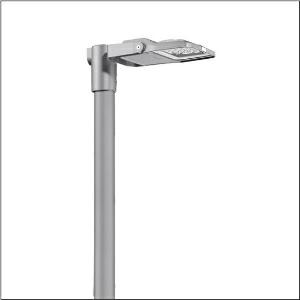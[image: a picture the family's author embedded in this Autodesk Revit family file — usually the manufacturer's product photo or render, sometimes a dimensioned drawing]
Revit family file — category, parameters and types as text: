
# Revit family: floodlight_fl_21_iq_micro___pl43_5xa7761a4a3a_9f97
name_source: partatom
category: Lighting Fixtures
units: mm (PartAtom-declared; Revit-internal decimal feet)

## family parameters
Cut with Voids When Loaded = No
Host = Face
Light Source = No
Part Type = Normal
Room Calculation Point = No
Round Connector Dimension = Use Diameter
Shared = No

## types (1)
- --- (1 x LED, 3170 lm, 23.1 W, 4000K)
    Apparent Load = 23 VA
    CIE Flux Codes = 29 80 99 100 100
    Color Rendering = 70
    Color Temperature = 4000K
    Default Elevation = 1800 mm
    Description = Floodlight FL 21 iQ micro, floodlight, primary light control with lens, of PMMA, primary optical cover: protective disc, of toughened safety glass, transparent, light distribution: PL43, light emission: direct distribution, installation type: surface-mounted, LED, High Power LED, rated luminous flux: 3.170lm, luminous efficacy: 137lm/W, light colour: 740, colour temperature: 4000K, control: optimised constant luminous flux control (CLO 2.0), Desk-Remote (wireless, voltage-free reading and setting of iQ features in the workshop via application-optimized NFC function/RFID function), Light-Fading, Smart-Wire, Night-Set, Lumen-Switch, Temp-Guard, Auto-Match, with terminal, 6-pole, mains connection: 220..240V, AC, 50/60Hz, start of lifetime: 23W, end of service life: 24W, reduction: 11W, luminaire housing, of diecast aluminium, powder-coated, Siteco® metallic grey (DB 702S), corrosivity category C5 mid according to DIN EN ISO 12944, sealing non-destructively replaceable, please order mast flange separately, mast bracket, of steel, galvanised, powder-coated, Siteco® metallic grey (DB 702S), protection rating (complete): IP66, insulation class (complete): insulation class II (safety insulation), certification: CE, ENEC, VDE, protection symbol: D, impact resistance: IK07, permissible operating ambient temperature: -40..+40°C, permissible operating ambient temperature for outdoor applications: -40..+50°C, standard: DIN EN 12944, LABS conformity tested according to VDMA 24364:2018-05, packaging unit: 1 piece

Light Distribution: PL43
    Height = 65 mm
    Lamp = 1 x LED
    Lamp Light Flux = 3170 lm
    Lamp Power = 23.1 W
    Lamp count = 1
    Length = 312 mm
    Luminous efficacy = 137 lm/W
    Manufacturer = Siteco
    ModVariant = No
    Model = 5XA7761A4A3A
    Number of Poles = 1
    OnlyDefault = Yes
    Power Factor = 1
    Product Name = Floodlight FL 21 iQ micro | PL43
    Product group = floodlight | pylon annexe
    ProductGroupID = 6200
    Protection Class = Protection class II
    Protection Degree = IP 66
    RLX_Detail_Level = 1
    RLX_Emergency_Light_Flux = 0 lm
    RLX_Emergency_Type = 0
    RLX_Emergency_Type_DB = No
    RlxData = <blob elided: 101741 chars, md5=c756d3e8>
    Socket = socket
    Standby Power = 0 W
    System Light Flux = 3170 lm
    System Power = 23 W
    Type Comments = factory setting: luminous flux: 100 % | dim-lin: 254 | 455 mA
    Type Image = l_1007121.jpg
    URL = http://relux.com
    VarID = @adj_147983
    Voltage = 0 V
    Weight = 0.00 kg
    Width = 230 mm

## geometry (parser evidence)
native form markers: Blend x4, Sweep x11
no freeform markers — native parametric forms only
